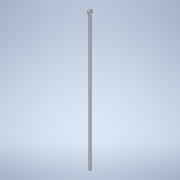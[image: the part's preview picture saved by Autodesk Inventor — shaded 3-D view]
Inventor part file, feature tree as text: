
AUTODESK INVENTOR PART (.ipt)
format: ipt  version: 2020 (Build 240168000, 168)  size: 119,808 bytes
history: native  units: mm
features: extrude x2, sketch x2
ambient origin geometry x8: Origin, YZ Plane, XZ Plane, XY Plane, X Axis, Y Axis, Z Axis, Center Point
bodies: Body1 (feature_tree)
feature tree (4):
  extrude  "Extrusion2"  Depth=2.0mm
  extrude  "Extrusion4"  Depth=2.4mm
  sketch  "Sketch4"  dims[d10=280.0mm d11=2.0mm]
  sketch  "Sketch6"  dims[d12=5.25mm d13=9.0mm d14=2.4mm d15=0.0mm d19=5.0mm d20=0.0mm d17=0.5mm d18=0.872665mm]
